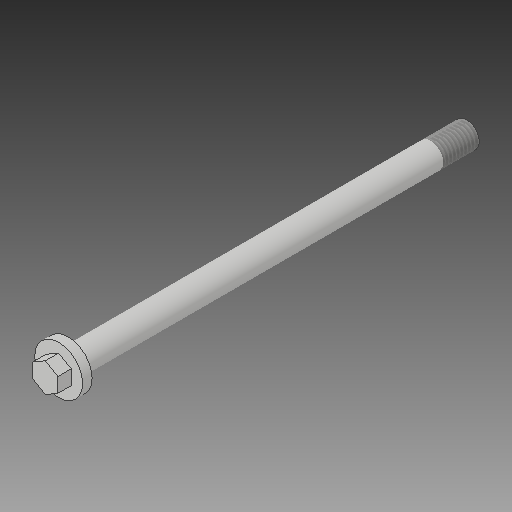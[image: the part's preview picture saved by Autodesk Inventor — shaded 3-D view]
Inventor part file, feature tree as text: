
AUTODESK INVENTOR PART (.ipt)
format: ipt  version: 2018 (Build 220112000, 112)  size: 111,104 bytes
history: native  units: mm
features: extrude x3, sketch x3, other x1, thread x1
ambient origin geometry x8: Origin, YZ Plane, XZ Plane, XY Plane, X Axis, Y Axis, Z Axis, Center Point
bodies: Body1 (feature_tree)
feature tree (8):
  other  "ソリッド1"
  extrude  "押し出し1"  Depth=11.9mm
  thread  "ねじ1"
  extrude  "押し出し2"  Depth=188.0mm TaperAngle=0.0deg
  extrude  "押し出し3"  Depth=17.0mm TaperAngle=0.0deg
  sketch  "スケッチ1"
  sketch  "スケッチ3"
  sketch  "スケッチ4"
